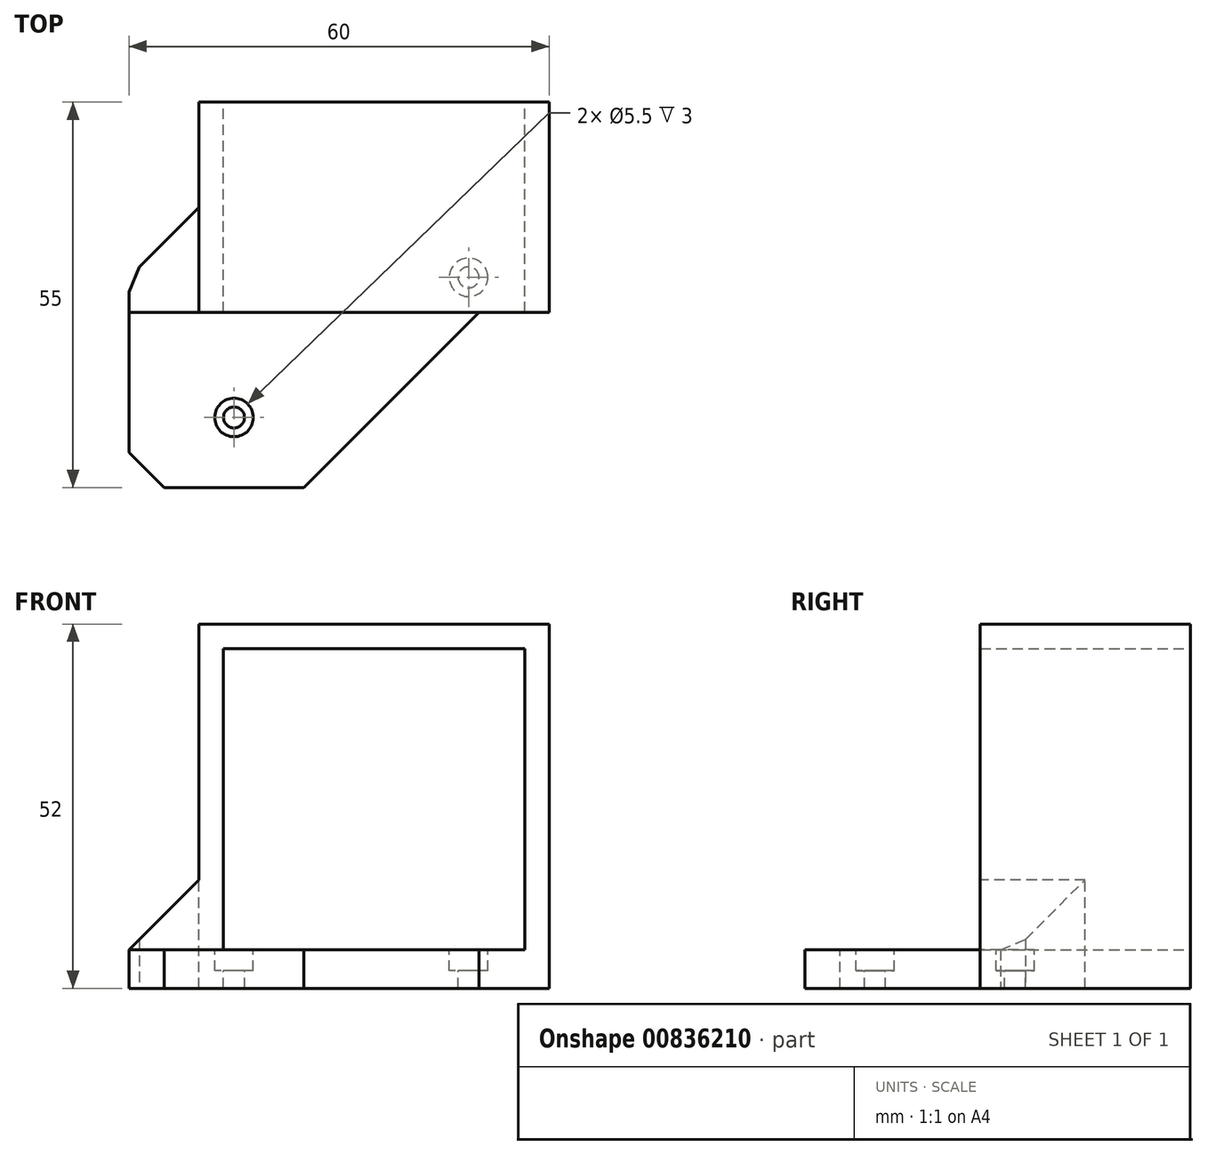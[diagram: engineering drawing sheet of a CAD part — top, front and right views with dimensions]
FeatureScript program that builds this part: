
annotation { "Feature Type Name" : "Feature", "Feature Type Description" : "" }
export const myFeature = defineFeature(function(context is Context, id is Id, definition is map)
    precondition{}
    {
        {
            var Q0;
            Q0=qCreatedBy(makeId("Front.planeOp"),FACE);
            var sketch = newSketch(context, id + "F0", { "sketchPlane" : qUnion([Q0])});
            skLineSegment(sketch, "E0.bottom", {"start": v(25, -27) * mm, "end": v(-25, -27) * mm});
            skLineSegment(sketch, "E0.top", {"start": v(25, 25) * mm, "end": v(-25, 25) * mm});
            skLineSegment(sketch, "E0.left", {"start": v(25, -27) * mm, "end": v(25, 25) * mm});
            skLineSegment(sketch, "E0.right", {"start": v(-25, -27) * mm, "end": v(-25, 25) * mm});
            skPoint(sketch, "E0.middle", {"position": v(0, -1) * mm});
            skSolve(sketch);
        }
        {
            var Q0;
            Q0=makeQuery(id+"F0.imprint","IMPRINT",FACE,{"disambiguationData":[TD([[makeQuery(id+"F0.imprint","IMPRINT",EDGE,{"derivedFrom":sQuery(id+"F0.wireOp",EDGE,"E0.bottom")}),-1.0]])]});
            var sketch = newSketch(context, id + "F1", { "sketchPlane" : qUnion([Q0])});
            skLineSegment(sketch, "E1.bottom", {"start": v(21.5, -21.5) * mm, "end": v(-21.5, -21.5) * mm});
            skLineSegment(sketch, "E1.top", {"start": v(21.5, 21.5) * mm, "end": v(-21.5, 21.5) * mm});
            skLineSegment(sketch, "E1.left", {"start": v(21.5, -21.5) * mm, "end": v(21.5, 21.5) * mm});
            skLineSegment(sketch, "E1.right", {"start": v(-21.5, -21.5) * mm, "end": v(-21.5, 21.5) * mm});
            skPoint(sketch, "E1.middle", {"position": v(0, 0) * mm});
            skSolve(sketch);
        }
        {
            var Q0;
            Q0 = qSketchRegion(id + "F0", true);
            extrude(context, id + "F2", {"entities" : qUnion([Q0]), "depth" : 30 * mm, "offsetDistance" : 25 * mm});
        }
        {
            var Q0;
            Q0 = qSketchRegion(id + "F1", true);
            extrude(context, id + "F3", {"entities" : qUnion([Q0]), "operationType" : NewBodyOperationType.REMOVE, "depth" : 30 * mm, "offsetDistance" : 25 * mm});
        }
        {
            var Q0;
            Q0=makeQuery(id+"F2.opExtrude","CAP_FACE",FACE,{"disambiguationData":[OSD([sQuery(id+"F0.wireOp",EDGE,"E0.bottom"),sQuery(id+"F0.wireOp",EDGE,"E0.top"),sQuery(id+"F0.wireOp",EDGE,"E0.left"),sQuery(id+"F0.wireOp",EDGE,"E0.right")])],"isStart":false});
            var sketch = newSketch(context, id + "F4", { "sketchPlane" : qUnion([Q0])});
            skLineSegment(sketch, "E2.bottom", {"start": v(-25, -27) * mm, "end": v(-15, -27) * mm});
            skLineSegment(sketch, "E2.top", {"start": v(-25, -21.5) * mm, "end": v(-15, -21.5) * mm});
            skLineSegment(sketch, "E2.left", {"start": v(-25, -27) * mm, "end": v(-25, -21.5) * mm});
            skLineSegment(sketch, "E2.right", {"start": v(-15, -27) * mm, "end": v(-15, -21.5) * mm});
            skSolve(sketch);
        }
        {
            var Q0;
            Q0=makeQuery(id+"F3.boolean.opBoolean","COPY",FACE,{"derivedFrom":makeQuery(id+"F3.opExtrude","SWEPT_FACE",FACE,{"disambiguationData":[OSD([sQuery(id+"F1.wireOp",EDGE,"E1.bottom")])]})});
            var sketch = newSketch(context, id + "F5", { "sketchPlane" : qUnion([Q0])});
            skLineSegment(sketch, "E3.bottom", {"start": v(5, -25) * mm, "end": v(-35, -25) * mm});
            skLineSegment(sketch, "E3.top", {"start": v(5, -55) * mm, "end": v(-35, -55) * mm});
            skLineSegment(sketch, "E3.left", {"start": v(5, -25) * mm, "end": v(5, -55) * mm});
            skLineSegment(sketch, "E3.right", {"start": v(-35, -25) * mm, "end": v(-35, -55) * mm});
            skSolve(sketch);
        }
        {
            var Q0;
            Q0 = qSketchRegion(id + "F5", true);
            extrude(context, id + "F6", {"entities" : qUnion([Q0]), "operationType" : NewBodyOperationType.ADD, "oppositeDirection" : true, "depth" : 5.5 * mm, "offsetDistance" : 25 * mm});
        }
        {
            var Q0;
            Q0 = qSketchRegion(id + "F4", true);
            extrude(context, id + "F7", {"entities" : qUnion([Q0]), "operationType" : NewBodyOperationType.ADD, "depth" : 20 * mm, "offsetDistance" : 25 * mm});
        }
        {
            var Q0;
            Q0=makeQuery(id+"F7.boolean.opBoolean","MERGE",FACE,{"derivedFrom":[makeQuery(id+"F3.boolean.opBoolean","COPY",FACE,{"derivedFrom":makeQuery(id+"F3.opExtrude","SWEPT_FACE",FACE,{"disambiguationData":[OSD([sQuery(id+"F1.wireOp",EDGE,"E1.bottom")])]})}),makeQuery(id+"F7.opExtrude","SWEPT_FACE",FACE,{"disambiguationData":[OSD([sQuery(id+"F4.wireOp",EDGE,"E2.top")])]})]});
            var sketch = newSketch(context, id + "F8", { "sketchPlane" : qUnion([Q0])});
            skCircle(sketch, "E4", {"center": v(-20, -45) * mm, "radius": 1.5 * mm});
            skCircle(sketch, "E5", {"center": v(13.5, -25) * mm, "radius": 1.5 * mm});
            skLineSegment(sketch, "E6", {"start": v(13.5, -25) * mm, "end": v(13.5, -45) * mm, "construction": true});
            skSolve(sketch);
        }
        {
            var Q0;
            Q0 = qSketchRegion(id + "F8", true);
            extrude(context, id + "F9", {"entities" : qUnion([Q0]), "operationType" : NewBodyOperationType.REMOVE, "oppositeDirection" : true, "depth" : 25 * mm, "offsetDistance" : 25 * mm});
        }
        {
            var Q0;
            Q0=makeQuery(id+"F7.boolean.opBoolean","MERGE",FACE,{"derivedFrom":[makeQuery(id+"F3.boolean.opBoolean","COPY",FACE,{"derivedFrom":makeQuery(id+"F3.opExtrude","SWEPT_FACE",FACE,{"disambiguationData":[OSD([sQuery(id+"F1.wireOp",EDGE,"E1.bottom")])]})}),makeQuery(id+"F7.opExtrude","SWEPT_FACE",FACE,{"disambiguationData":[OSD([sQuery(id+"F4.wireOp",EDGE,"E2.top")])]})]});
            var sketch = newSketch(context, id + "F10", { "sketchPlane" : qUnion([Q0])});
            skCircle(sketch, "E7", {"center": v(-20, -45) * mm, "radius": 2.75 * mm});
            skCircle(sketch, "E8", {"center": v(13.5, -25) * mm, "radius": 2.75 * mm});
            skSolve(sketch);
        }
        {
            var Q0;
            Q0 = qSketchRegion(id + "F10", true);
            extrude(context, id + "F11", {"entities" : qUnion([Q0]), "operationType" : NewBodyOperationType.REMOVE, "oppositeDirection" : true, "depth" : 3 * mm, "offsetDistance" : 25 * mm});
        }
        {
            var Q0;
            Q0=makeQuery(id+"F6.boolean.opBoolean","INTERSECT",EDGE,{"derivedFrom":[makeQuery(id+"F2.opExtrude","SWEPT_FACE",FACE,{"disambiguationData":[OSD([sQuery(id+"F0.wireOp",EDGE,"E0.right")])]}),makeQuery(id+"F6.opExtrude","SWEPT_FACE",FACE,{"disambiguationData":[OSD([sQuery(id+"F5.wireOp",EDGE,"E3.bottom")])]})]});
            var Q1;
            Q1=makeQuery(id+"F6.boolean.opBoolean","INTERSECT",EDGE,{"derivedFrom":[makeQuery(id+"F2.opExtrude","SWEPT_FACE",FACE,{"disambiguationData":[OSD([sQuery(id+"F0.wireOp",EDGE,"E0.right")])]}),makeQuery(id+"F6.opExtrude","CAP_FACE",FACE,{"disambiguationData":[OSD([sQuery(id+"F5.wireOp",EDGE,"E3.bottom"),sQuery(id+"F5.wireOp",EDGE,"E3.top"),sQuery(id+"F5.wireOp",EDGE,"E3.left"),sQuery(id+"F5.wireOp",EDGE,"E3.right")])],"isStart":true})]});
            var Q2;
            Q2=makeQuery(id+"F6.boolean.opBoolean","INTERSECT",EDGE,{"derivedFrom":[makeQuery(id+"F2.opExtrude","CAP_FACE",FACE,{"disambiguationData":[OSD([sQuery(id+"F0.wireOp",EDGE,"E0.bottom"),sQuery(id+"F0.wireOp",EDGE,"E0.top"),sQuery(id+"F0.wireOp",EDGE,"E0.left"),sQuery(id+"F0.wireOp",EDGE,"E0.right")])],"isStart":false}),makeQuery(id+"F6.opExtrude","SWEPT_FACE",FACE,{"disambiguationData":[OSD([sQuery(id+"F5.wireOp",EDGE,"E3.left")])]})]});
            chamfer(context, id + "F12", {"entities" : qUnion([Q0, Q1, Q2]), "width" : 10 * mm, "tangentPropagation" : true});
        }
        {
            var Q0;
            Q0=makeQuery(id+"F6.opExtrude","SWEPT_EDGE",EDGE,{"disambiguationData":[OSD([sQuery(id+"F5.wireOp",EDGE,"E3.top"),sQuery(id+"F5.wireOp",EDGE,"E3.left")])]});
            chamfer(context, id + "F13", {"entities" : qUnion([Q0]), "width" : 15 * mm, "tangentPropagation" : true});
        }
        {
            var Q0;
            Q0=makeQuery(id+"F6.opExtrude","SWEPT_EDGE",EDGE,{"disambiguationData":[OSD([sQuery(id+"F5.wireOp",EDGE,"E3.top"),sQuery(id+"F5.wireOp",EDGE,"E3.right")])]});
            chamfer(context, id + "F14", {"entities" : qUnion([Q0]), "width" : 5 * mm, "tangentPropagation" : true});
        }
        {
            var Q0;
            Q0=makeQuery(id+"F12.opChamfer","BLEND_EDGE",EDGE,{"blendedFrom":[makeQuery(id+"F6.boolean.opBoolean","INTERSECT",EDGE,{"derivedFrom":[makeQuery(id+"F2.opExtrude","SWEPT_FACE",FACE,{"disambiguationData":[OSD([sQuery(id+"F0.wireOp",EDGE,"E0.right")])]}),makeQuery(id+"F6.opExtrude","SWEPT_FACE",FACE,{"disambiguationData":[OSD([sQuery(id+"F5.wireOp",EDGE,"E3.bottom")])]})]}),makeQuery(id+"F6.opExtrude","SWEPT_FACE",FACE,{"disambiguationData":[OSD([sQuery(id+"F5.wireOp",EDGE,"E3.right")])]})],"blendedInto":[makeQuery(id+"F6.opExtrude","SWEPT_FACE",FACE,{"disambiguationData":[OSD([sQuery(id+"F5.wireOp",EDGE,"E3.right")])]})]});
            chamfer(context, id + "F15", {"entities" : qUnion([Q0]), "width" : 5 * mm, "tangentPropagation" : true});
        }
    });
